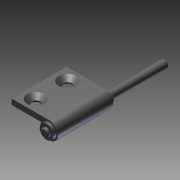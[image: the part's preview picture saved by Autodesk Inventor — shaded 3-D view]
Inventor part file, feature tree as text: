
AUTODESK INVENTOR PART (.ipt)
format: ipt  version: 2011 SP1 (Build 150282100, 282)  size: 130,560 bytes
history: native  units: mm
features: other x35, sketch x4, hole x2, revolve x1, extrude x1
ambient origin geometry x8: Origin, YZ Plane, XZ Plane, XY Plane, X Axis, Y Axis, Z Axis, Center Point
bodies: Solid1 (feature_tree)
feature tree (43):
  revolve  "Revolution1"  [1 undecoded]
  extrude  "Extrusion1"  TaperAngle=0.0deg  [1 undecoded]
  hole  "Hole1"  [1 undecoded]
  hole  "Hole2"  [1 undecoded]
  other  "1_XY"
  other  "1_YZ"
  other  "1_ZX"
  other  "1_X"
  other  "1_Y"
  other  "1_Z"
  other  "1_Center"
  other  "to_bolt1_XY"
  other  "to_bolt1_YZ"
  other  "to_bolt1_ZX"
  other  "to_bolt1_X"
  other  "to_bolt1_Y"
  other  "to_bolt1_Z"
  other  "to_bolt1_Center"
  other  "to_bolt1_r_XY"
  other  "to_bolt1_r_YZ"
  other  "to_bolt1_r_ZX"
  other  "to_bolt1_r_X"
  other  "to_bolt1_r_Y"
  other  "to_bolt1_r_Z"
  other  "to_bolt1_r_Center"
  other  "to_bolt2_XY"
  other  "to_bolt2_YZ"
  other  "to_bolt2_ZX"
  other  "to_bolt2_X"
  other  "to_bolt2_Y"
  other  "to_bolt2_Z"
  other  "to_bolt2_Center"
  other  "to_bolt2_r_XY"
  other  "to_bolt2_r_YZ"
  other  "to_bolt2_r_ZX"
  other  "to_bolt2_r_X"
  other  "to_bolt2_r_Y"
  other  "to_bolt2_r_Z"
  other  "to_bolt2_r_Center"
  sketch  "Sketch_1"  dims[d0=360.0deg d1=3.5mm d2=0.0mm]
  sketch  "Sketch_3"  dims[d3=5.5mm d4=6.0mm d5=11.0mm d6=2.0mm d7=90.0deg d8=3.5mm d9=0.0mm]
  sketch  "Sketch3"  dims[d10=5.5mm d11=6.0mm d12=11.0mm d13=2.0mm d14=90.0deg d15=3.5mm d16=0.0mm d17=0.0mm d18=0.0mm d19=0.0mm]
  sketch  "Sketch4"
note: 4 required parameter values undecoded (feature->parameter linkage not recoverable at this tier; creation-order binding heuristic only, values carry confidence <= 0.55)